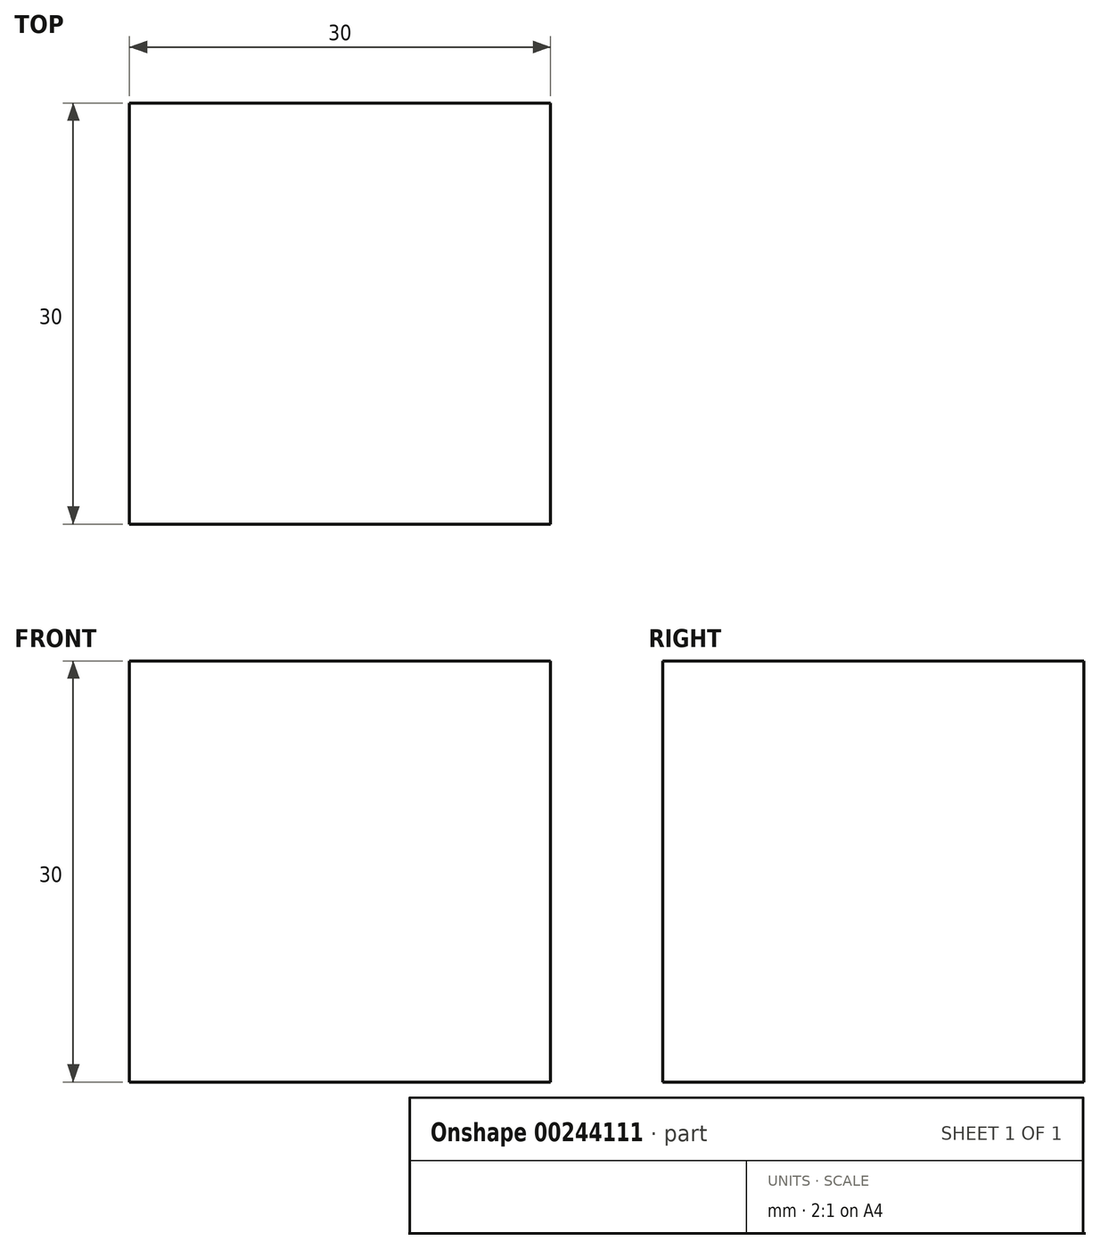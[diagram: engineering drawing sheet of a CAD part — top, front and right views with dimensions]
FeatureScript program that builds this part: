
annotation { "Feature Type Name" : "Feature", "Feature Type Description" : "" }
export const myFeature = defineFeature(function(context is Context, id is Id, definition is map)
    precondition{}
    {
        {
            var Q0;
            Q0=qCreatedBy(makeId("Right.planeOp"),FACE);
            var sketch = newSketch(context, id + "F0", { "sketchPlane" : qUnion([Q0])});
            skLineSegment(sketch, "E0.bottom", {"start": v(-21.86, -18.05) * mm, "end": v(-51.86, -18.05) * mm});
            skLineSegment(sketch, "E0.top", {"start": v(-21.86, -48.05) * mm, "end": v(-51.86, -48.05) * mm});
            skLineSegment(sketch, "E0.left", {"start": v(-21.86, -18.05) * mm, "end": v(-21.86, -48.05) * mm});
            skLineSegment(sketch, "E0.right", {"start": v(-51.86, -18.05) * mm, "end": v(-51.86, -48.05) * mm});
            skSolve(sketch);
        }
        {
            var Q0;
            Q0=makeQuery(id+"F0.imprint","IMPRINT",FACE,{"disambiguationData":[TD([[makeQuery(id+"F0.imprint","IMPRINT",EDGE,{"derivedFrom":sQuery(id+"F0.wireOp",EDGE,"E0.bottom")}),1.0]])]});
            extrude(context, id + "F1", {"entities" : qUnion([Q0]), "offsetDistance" : 25 * mm, "depth" : 30 * mm});
        }
    });
